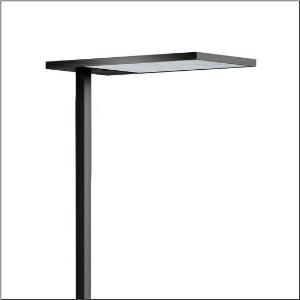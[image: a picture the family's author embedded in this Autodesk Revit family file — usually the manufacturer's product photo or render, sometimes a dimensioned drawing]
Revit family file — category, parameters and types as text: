
# Revit family: silica_r__21_floor_r_51mx53sg4db_4ec3
name_source: partatom
category: Lighting Fixtures
units: mm (PartAtom-declared; Revit-internal decimal feet)

## family parameters
Cut with Voids When Loaded = No
Host = Face
Light Source = No
Part Type = Normal
Room Calculation Point = No
Round Connector Dimension = Use Diameter
Shared = No

## types (1)
- Silica® 21 Floor R (1 x LED, 15000 lm, 106.4 W, 4000K)
    Apparent Load = 106 VA
    CIE Flux Codes = 54 86 97 13 100
    Color Rendering = 80
    Color Temperature = 4000K
    Default Elevation = 1800 mm
    Description = Silica® 21 Floor R, floorstanding luminaire, of PMMA, primary optical cover: prismatic diffuser, of PMMA, CAT 2 (L<= 3000cd/m²), light emission: indirect/direct distribution, primary light characteristic: symmetric, primary optical cover: cover panel, of PMMA, installation type: not mounted, LED, rated luminous flux: 15.000lm, luminous efficacy: 141lm/W, light colour: 840, colour temperature: 4000K, control gear: DALI 2, daylight-dependent control, mains connection: 230V, AC, 50/60Hz, connection cable included, cable length: 2,5m, rated input power: 106.4W, luminaire head, of aluminium, powder-coated, jet black (RAL 9005), length: 671mm, width: 371mm, height: 2010mm, supporting column, angular, of aluminium, powder-coated, jet black (RAL 9005), baseplate, of steel, powder-coated, jet black (RAL 9005), sensor module PR3-S, local control - self-sufficient standalone sensors, equipment: master, dimmable, protection rating (complete): IP20, insulation class (complete): insulation class I (protective earthing), certification: CE, standard: EN 50419, packaging unit: 1 piece
    Height = 18 mm
    Lamp = 1 x LED
    Lamp Light Flux = 15000 lm
    Lamp Power = 106.4 W
    Lamp count = 1
    Length = 650 mm
    Luminous efficacy = 141 lm/W
    Manufacturer = Siteco
    ModVariant = No
    Model = 51MX53SG4DB
    Mounting Place = Floor
    Mounting Type = Freestanding
    Number of Poles = 1
    OnlyDefault = Yes
    Power Factor = 1
    Product Name = Silica® 21 Floor R
    Product group = floorstanding luminaire
    ProductGroupID = 1302
    Protection Class = Protection class I
    Protection Degree = IP 20
    RLX_Detail_Level = 1
    RLX_Emergency_Light_Flux = 0 lm
    RLX_Emergency_Type = 0
    RLX_Emergency_Type_DB = No
    RlxData = <blob elided: 22261 chars, md5=0b8bb7e2>
    Socket = socket
    Standby Power = 0 W
    System Light Flux = 15000 lm
    System Power = 106 W
    Type Comments = Product without accessories
    Type Image = l_1007011.jpg
    URL = http://relux.com
    VarID = ---
    Voltage = 0 V
    Weight = 0.00 kg
    Width = 350 mm

## geometry (parser evidence)
native form markers: Blend x4, Sweep x16
no freeform markers — native parametric forms only
